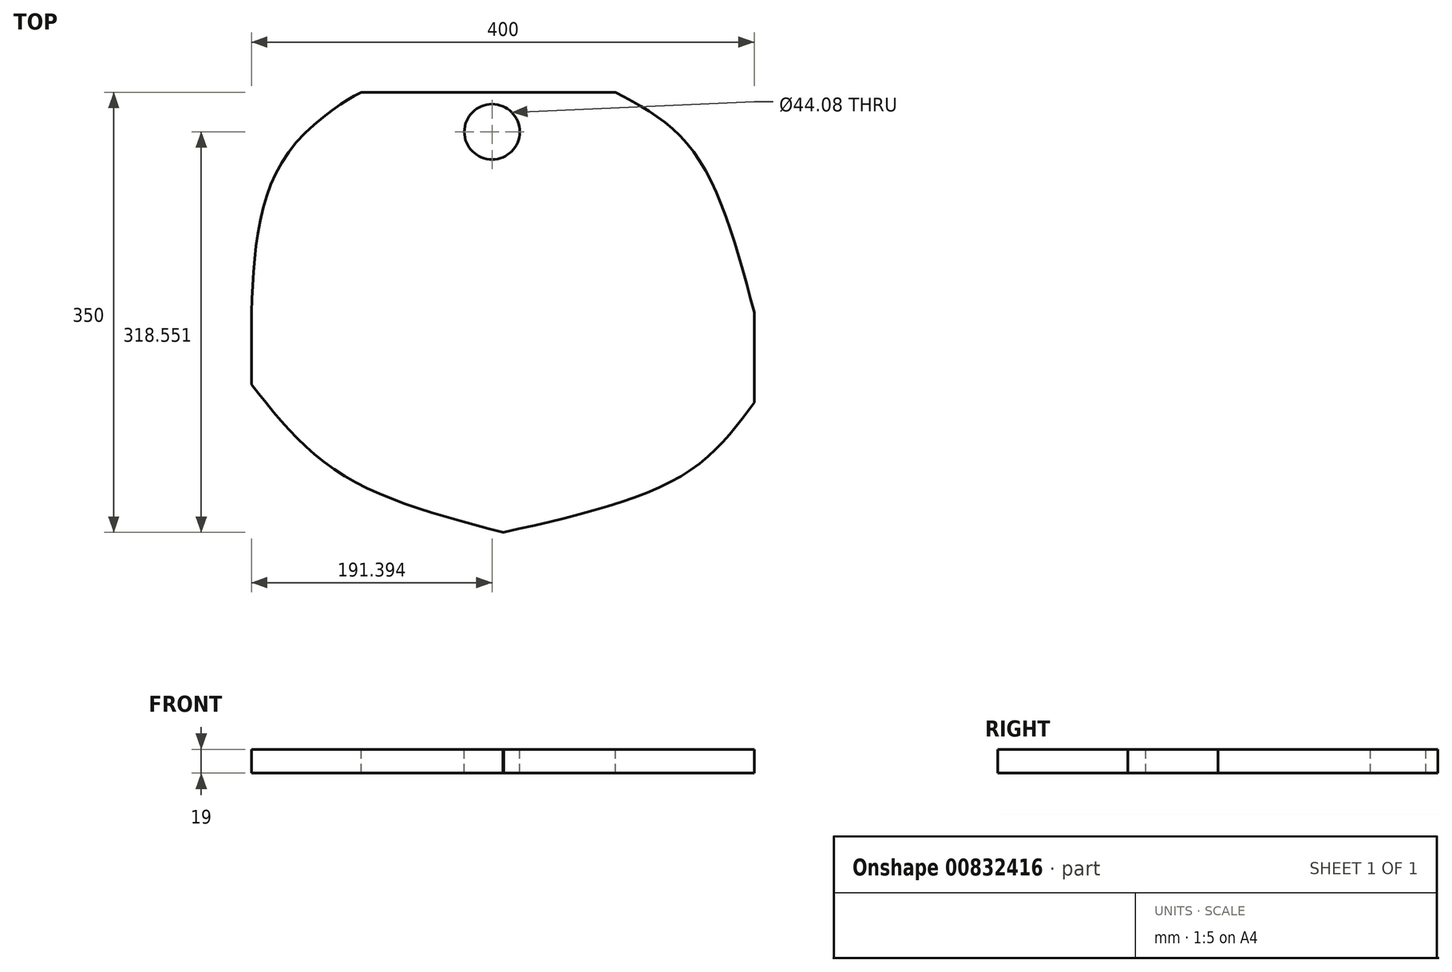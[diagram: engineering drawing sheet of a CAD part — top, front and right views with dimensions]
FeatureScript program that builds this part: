
annotation { "Feature Type Name" : "Feature", "Feature Type Description" : "" }
export const myFeature = defineFeature(function(context is Context, id is Id, definition is map)
    precondition{}
    {
        {
            var Q0;
            Q0=qCreatedBy(makeId("Top.planeOp"),FACE);
            var sketch = newSketch(context, id + "F0", { "sketchPlane" : qUnion([Q0])});
            skLineSegment(sketch, "E0.bottom", {"start": v(200, -175) * mm, "end": v(-200, -175) * mm});
            skLineSegment(sketch, "E0.top", {"start": v(200, 175) * mm, "end": v(-200, 175) * mm});
            skLineSegment(sketch, "E0.left", {"start": v(200, -175) * mm, "end": v(200, 175) * mm});
            skLineSegment(sketch, "E0.right", {"start": v(-200, -175) * mm, "end": v(-200, 175) * mm});
            skPoint(sketch, "E0.middle", {"position": v(0, 0) * mm});
            skSolve(sketch);
        }
        {
            var Q0;
            Q0=makeQuery(id+"F0.imprint","IMPRINT",FACE,{"disambiguationData":[TD([[makeQuery(id+"F0.imprint","IMPRINT",EDGE,{"derivedFrom":sQuery(id+"F0.wireOp",EDGE,"E0.bottom")}),-1.0]])]});
            extrude(context, id + "F1", {"entities" : qUnion([Q0]), "depth" : 19 * mm, "offsetDistance" : 25 * mm});
        }
        {
            var Q0;
            Q0=makeQuery(id+"F1.opExtrude","CAP_FACE",FACE,{"disambiguationData":[OSD([sQuery(id+"F0.wireOp",EDGE,"E0.bottom"),sQuery(id+"F0.wireOp",EDGE,"E0.top"),sQuery(id+"F0.wireOp",EDGE,"E0.left"),sQuery(id+"F0.wireOp",EDGE,"E0.right")])],"isStart":false});
            var sketch = newSketch(context, id + "F2", { "sketchPlane" : qUnion([Q0])});
            skFitSpline(sketch, "E1", {"points": [v(-200, 0) * mm, v(-169.32, 128.98) * mm, v(-112.59, 175) * mm, v(-112.03, 175) * mm], "startDerivative": vector(11.2, 255.2) * mm, "endDerivative": vector(9.28, -3.84) * mm});
            skSolve(sketch);
        }
        {
            var Q0;
            {var subQ0=sQuery(id+"F2.wireOp",EDGE,"E1");var subQ1=makeQuery(id+"F1.opExtrude","CAP_EDGE",EDGE,{"disambiguationData":[OSD([sQuery(id+"F0.wireOp",EDGE,"E0.right")])],"isStart":false});var subQ2=makeQuery(id+"F2.imprint","INTERSECT",VERTEX,{"derivedFrom":[subQ1,subQ0]});Q0=makeQuery(id+"F2.imprint","IMPRINT",FACE,{"disambiguationData":[TD([[makeQuery(id+"F2.imprint","IMPRINT",EDGE,{"disambiguationData":[TD([[subQ2,-1.0]])],"derivedFrom":subQ0}),1.0]])]});}
            extrude(context, id + "F3", {"entities" : qUnion([Q0]), "operationType" : NewBodyOperationType.REMOVE, "endBound" : BoundingType.THROUGH_ALL, "oppositeDirection" : true, "depth" : 25 * mm, "offsetDistance" : 25 * mm});
        }
        {
            var Q0;
            Q0=makeQuery(id+"F1.opExtrude","CAP_FACE",FACE,{"disambiguationData":[OSD([sQuery(id+"F0.wireOp",EDGE,"E0.bottom"),sQuery(id+"F0.wireOp",EDGE,"E0.top"),sQuery(id+"F0.wireOp",EDGE,"E0.left"),sQuery(id+"F0.wireOp",EDGE,"E0.right")])],"isStart":false});
            var sketch = newSketch(context, id + "F4", { "sketchPlane" : qUnion([Q0])});
            skFitSpline(sketch, "E2", {"points": [v(200, 0) * mm, v(150.74, 129.12) * mm, v(89.67, 175) * mm], "startDerivative": vector(-69.44, 258.81) * mm, "endDerivative": vector(-155.44, 82.54) * mm});
            skSolve(sketch);
        }
        {
            var Q0;
            {var subQ0=sQuery(id+"F4.wireOp",EDGE,"E2");Q0=makeQuery(id+"F4.imprint","IMPRINT",FACE,{"disambiguationData":[TD([[makeQuery(id+"F4.imprint","IMPRINT",EDGE,{"derivedFrom":subQ0}),-1.0]])]});}
            extrude(context, id + "F5", {"entities" : qUnion([Q0]), "operationType" : NewBodyOperationType.REMOVE, "endBound" : BoundingType.THROUGH_ALL, "oppositeDirection" : true, "depth" : 25 * mm, "offsetDistance" : 25 * mm});
        }
        {
            var Q0;
            Q0=makeQuery(id+"F1.opExtrude","CAP_FACE",FACE,{"disambiguationData":[OSD([sQuery(id+"F0.wireOp",EDGE,"E0.bottom"),sQuery(id+"F0.wireOp",EDGE,"E0.top"),sQuery(id+"F0.wireOp",EDGE,"E0.left"),sQuery(id+"F0.wireOp",EDGE,"E0.right")])],"isStart":false});
            var sketch = newSketch(context, id + "F6", { "sketchPlane" : qUnion([Q0])});
            skFitSpline(sketch, "E3", {"points": [v(0, -175) * mm, v(-129.64, -127.95) * mm, v(-200, -57.44) * mm], "startDerivative": vector(-263.25, 69.07) * mm, "endDerivative": vector(-133.23, 168.75) * mm});
            skSolve(sketch);
        }
        {
            var Q0;
            {var subQ2=sQuery(id+"F6.wireOp",EDGE,"E3");Q0=makeQuery(id+"F6.imprint","IMPRINT",FACE,{"disambiguationData":[TD([[makeQuery(id+"F6.imprint","IMPRINT",EDGE,{"derivedFrom":subQ2}),-1.0]])]});}
            var sketch = newSketch(context, id + "F7", { "sketchPlane" : qUnion([Q0])});
            skFitSpline(sketch, "E4", {"points": [v(0, -175.15) * mm, v(144.63, -128.5) * mm, v(200.71, -70.76) * mm], "startDerivative": vector(283.69, 64.23) * mm, "endDerivative": vector(108.54, 148.98) * mm});
            skSolve(sketch);
        }
        {
            var Q0;
            {var subQ0=sQuery(id+"F6.wireOp",EDGE,"E3");Q0=makeQuery(id+"F6.imprint","IMPRINT",FACE,{"disambiguationData":[TD([[makeQuery(id+"F6.imprint","IMPRINT",EDGE,{"derivedFrom":subQ0}),1.0]])]});}
            var Q1;
            {var subQ0=sQuery(id+"F7.wireOp",EDGE,"E4");var subQ1=makeQuery(id+"F1.opExtrude","CAP_EDGE",EDGE,{"disambiguationData":[OSD([sQuery(id+"F0.wireOp",EDGE,"E0.left")])],"isStart":false});var subQ2=makeQuery(id+"F6.imprint","IMPRINT",EDGE,{"derivedFrom":subQ1});var subQ3=makeQuery(id+"F7.imprint","INTERSECT",VERTEX,{"derivedFrom":[subQ2,subQ0]});Q1=makeQuery(id+"F7.imprint","IMPRINT",FACE,{"disambiguationData":[TD([[makeQuery(id+"F7.imprint","IMPRINT",EDGE,{"disambiguationData":[TD([[subQ3,1.0]])],"derivedFrom":subQ0}),-1.0]])]});}
            extrude(context, id + "F8", {"entities" : qUnion([Q0, Q1]), "operationType" : NewBodyOperationType.REMOVE, "endBound" : BoundingType.THROUGH_ALL, "oppositeDirection" : true, "depth" : 25 * mm, "offsetDistance" : 25 * mm});
        }
        {
            var Q0;
            Q0=makeQuery(id+"F1.opExtrude","CAP_FACE",FACE,{"disambiguationData":[OSD([sQuery(id+"F0.wireOp",EDGE,"E0.bottom"),sQuery(id+"F0.wireOp",EDGE,"E0.top"),sQuery(id+"F0.wireOp",EDGE,"E0.left"),sQuery(id+"F0.wireOp",EDGE,"E0.right")])],"isStart":false});
            var sketch = newSketch(context, id + "F9", { "sketchPlane" : qUnion([Q0])});
            skCircle(sketch, "E5", {"center": v(-8.6, 143.55) * mm, "radius": 22.04 * mm});
            skSolve(sketch);
        }
        {
            var Q0;
            Q0=makeQuery(id+"F9.imprint","IMPRINT",FACE,{"disambiguationData":[TD([[makeQuery(id+"F9.imprint","IMPRINT",EDGE,{"derivedFrom":sQuery(id+"F9.wireOp",EDGE,"E5")}),1.0]])]});
            extrude(context, id + "F10", {"entities" : qUnion([Q0]), "operationType" : NewBodyOperationType.REMOVE, "endBound" : BoundingType.THROUGH_ALL, "oppositeDirection" : true, "depth" : 25 * mm, "offsetDistance" : 25 * mm});
        }
    });
